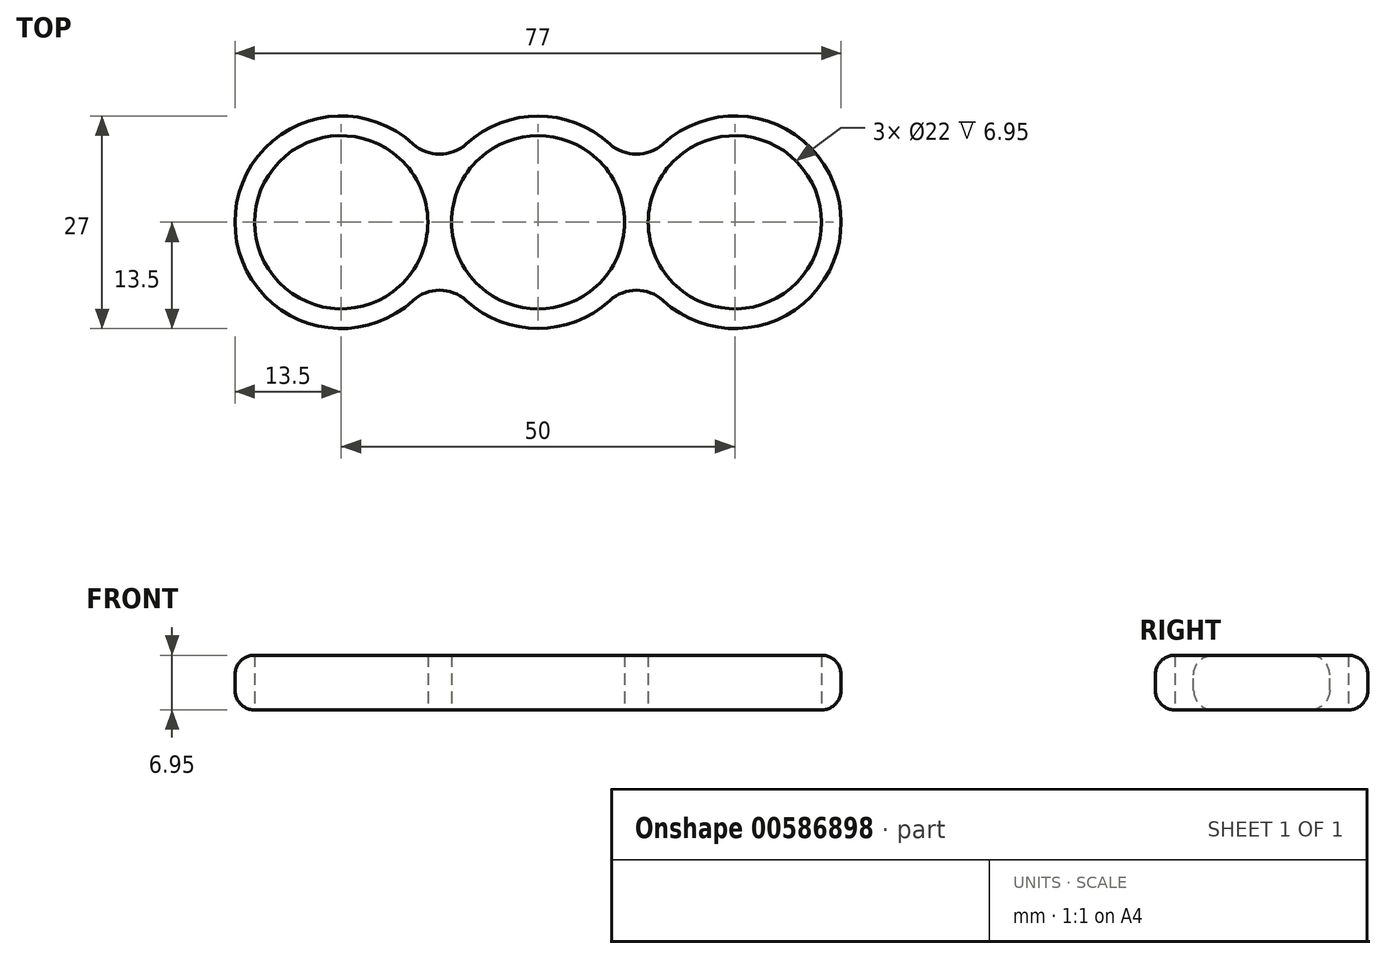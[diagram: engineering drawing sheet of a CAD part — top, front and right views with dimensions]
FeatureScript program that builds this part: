
annotation { "Feature Type Name" : "Feature", "Feature Type Description" : "" }
export const myFeature = defineFeature(function(context is Context, id is Id, definition is map)
    precondition{}
    {
        {
            var Q0;
            Q0=qCreatedBy(makeId("Top.planeOp"),FACE);
            var sketch = newSketch(context, id + "F0", { "sketchPlane" : qUnion([Q0])});
            skCircle(sketch, "E0", {"center": v(0, 0) * mm, "radius": 11 * mm});
            skArc(sketch, "E1", {"start": v(12.5, 5.1) * mm, "mid": v(0, 13.5) * mm, "end": v(-12.5, 5.1) * mm});
            skCircle(sketch, "E2", {"center": v(25, 0) * mm, "radius": 11 * mm});
            skArc(sketch, "E3", {"start": v(12.5, -5.1) * mm, "mid": v(38.5, 0) * mm, "end": v(12.5, 5.1) * mm});
            skArc(sketch, "E4.MirrorC", {"start": v(-12.5, -5.1) * mm, "mid": v(-38.5, 0) * mm, "end": v(-12.5, 5.1) * mm});
            skCircle(sketch, "E5.MirrorC", {"center": v(-25, 0) * mm, "radius": 11 * mm});
            skArc(sketch, "E6.trimOffspring", {"start": v(-12.5, -5.1) * mm, "mid": v(0, -13.5) * mm, "end": v(12.5, -5.1) * mm});
            skSolve(sketch);
        }
        {
            var Q0;
            Q0=makeQuery(id+"F0.imprint","IMPRINT",FACE,{"disambiguationData":[TD([[makeQuery(id+"F0.imprint","IMPRINT",EDGE,{"derivedFrom":sQuery(id+"F0.wireOp",EDGE,"E0")}),-1.0]])]});
            extrude(context, id + "F1", {"entities" : qUnion([Q0]), "depth" : 6.95 * mm, "offsetDistance" : 25 * mm});
        }
        {
            var Q0;
            Q0=makeQuery(id+"F1.opExtrude","SWEPT_EDGE",EDGE,{"disambiguationData":[OSD([sQuery(id+"F0.wireOp",EDGE,"E4.MirrorC"),sQuery(id+"F0.wireOp",EDGE,"E6.trimOffspring")])]});
            var Q1;
            Q1=makeQuery(id+"F1.opExtrude","SWEPT_EDGE",EDGE,{"disambiguationData":[OSD([sQuery(id+"F0.wireOp",EDGE,"E3"),sQuery(id+"F0.wireOp",EDGE,"E6.trimOffspring")])]});
            var Q2;
            Q2=makeQuery(id+"F1.opExtrude","SWEPT_EDGE",EDGE,{"disambiguationData":[OSD([sQuery(id+"F0.wireOp",EDGE,"E1"),sQuery(id+"F0.wireOp",EDGE,"E3")])]});
            var Q3;
            Q3=makeQuery(id+"F1.opExtrude","SWEPT_EDGE",EDGE,{"disambiguationData":[OSD([sQuery(id+"F0.wireOp",EDGE,"E1"),sQuery(id+"F0.wireOp",EDGE,"E4.MirrorC")])]});
            fillet(context, id + "F2", {"entities" : qUnion([Q0, Q1, Q2, Q3]), "radius" : 5 * mm, "tangentPropagation" : true, "allowEdgeOverflow" : false});
        }
        {
            var Q0;
            Q0=makeQuery(id+"F1.opExtrude","CAP_EDGE",EDGE,{"disambiguationData":[OSD([sQuery(id+"F0.wireOp",EDGE,"E4.MirrorC")])],"isStart":false});
            var Q1;
            Q1=makeQuery(id+"F1.opExtrude","CAP_EDGE",EDGE,{"disambiguationData":[OSD([sQuery(id+"F0.wireOp",EDGE,"E4.MirrorC")])],"isStart":true});
            fillet(context, id + "F3", {"entities" : qUnion([Q0, Q1]), "radius" : 2.5 * mm, "tangentPropagation" : true, "allowEdgeOverflow" : false});
        }
    });
